FCSTD DOCUMENT  (FreeCAD 0.21R33771 (Git))
Label: ex94
License: All rights reserved
LicenseURL: http://en.wikipedia.org/wiki/All_rights_reserved
objects: Sketcher::SketchObject×2, PartDesign::AdditiveLoft×1, PartDesign::Body×1
note: 5 computed .brp shape members not serialized (recipe doc carries the construction recipe); baked Part::Feature solids carry a one-line shape summary decoded from their .brp

FEATURE [Sketcher::SketchObject] Sketch
  FullyConstrained = false
  MapMode = 5
  Support = -> [XY_Plane]
  sketch-geometry (17):
    g0: LineSegment StartX=0 StartY=-24.175 StartZ=0 EndX=22.9918 EndY=-7.47049 EndZ=0
    g1: LineSegment StartX=22.9918 StartY=-7.47049 StartZ=0 EndX=14.2097 EndY=19.558 EndZ=0
    g2: LineSegment StartX=14.2097 StartY=19.558 StartZ=0 EndX=-14.2097 EndY=19.558 EndZ=0
    g3: LineSegment StartX=-14.2097 StartY=19.558 StartZ=0 EndX=-22.9918 EndY=-7.47049 EndZ=0
    g4: LineSegment StartX=-22.9918 StartY=-7.47049 StartZ=0 EndX=0 EndY=-24.175 EndZ=0
    g5: Circle CenterX=0 CenterY=0 CenterZ=0 NormalX=0 NormalY=0 NormalZ=1 AngleXU=0 Radius=24.175
    g6: LineSegment StartX=-14.2097 StartY=19.558 StartZ=0 EndX=-1.8e-15 EndY=66.3733 EndZ=0
    g7: LineSegment StartX=-1.8e-15 StartY=66.3733 StartZ=0 EndX=14.2097 EndY=19.558 EndZ=0
    g8: LineSegment StartX=14.2097 StartY=19.558 StartZ=0 EndX=63.1247 EndY=20.5105 EndZ=0
    g9: LineSegment StartX=63.1247 StartY=20.5105 StartZ=0 EndX=22.9918 EndY=-7.47049 EndZ=0
    g10: LineSegment StartX=-14.2097 StartY=19.558 StartZ=0 EndX=-63.1247 EndY=20.5105 EndZ=0
    g11: LineSegment StartX=-63.1247 StartY=20.5105 StartZ=0 EndX=-22.9918 EndY=-7.47049 EndZ=0
    g12: LineSegment StartX=-22.9918 StartY=-7.47049 StartZ=0 EndX=-39.0132 EndY=-53.6971 EndZ=0
    g13: LineSegment StartX=-39.0132 StartY=-53.6971 StartZ=0 EndX=0 EndY=-24.175 EndZ=0
    g14: LineSegment StartX=0 StartY=-24.175 StartZ=0 EndX=39.0132 EndY=-53.6971 EndZ=0
    g15: LineSegment StartX=22.9918 StartY=-7.47049 StartZ=0 EndX=39.0132 EndY=-53.6971 EndZ=0
    g16: Circle CenterX=0 CenterY=0 CenterZ=0 NormalX=0 NormalY=0 NormalZ=1 AngleXU=0 Radius=66.3733
  constraints (39):
    c: Coincident(g0,g1)
    c: Coincident(g1,g2)
    c: Coincident(g2,g3)
    c: Coincident(g3,g4)
    c: Coincident(g4,g0)
    c: Equal(g0, g1-g4) x4
    c: PointOnObject(g0,g5)
    c: PointOnObject(g1,g5)
    c: PointOnObject(g2,g5)
    c: PointOnObject(g3,g5)
    c: PointOnObject(g4,g5)
    c: Coincident(g5,g-1)
    c: PointOnObject(g4,g-2)
    c: Coincident(g6,g2)
    c: PointOnObject(g6,g-2)
    c: Coincident(g7,g6)
    c: Coincident(g7,g1)
    c: Coincident(g8,g1)
    c: Coincident(g9,g8)
    c: Coincident(g9,g0)
    c: Coincident(g10,g2)
    c: Coincident(g11,g10)
    c: Coincident(g11,g3)
    c: Coincident(g12,g3)
    c: Coincident(g13,g12)
    c: Coincident(g13,g0)
    c: Coincident(g14,g0)
    c: Coincident(g15,g0)
    c: Coincident(g15,g14)
    c: Equal(g12,g13)
    c: Equal(g14,g15)
    c: Equal(g11,g10)
    c: Equal(g8,g9)
    c: Coincident(g16,g5)
    c: PointOnObject(g14,g16)
    c: PointOnObject(g8,g16)
    c: PointOnObject(g6,g16)
    c: PointOnObject(g10,g16)
    c: PointOnObject(g12,g16)
FEATURE [Sketcher::SketchObject] Sketch001
  AttachmentOffset = pos=(0,0,16) rot=(0,0,1;0rad)
  FullyConstrained = false
  MapMode = 5
  Placement = pos=(0,0,16) rot=(0,0,1;0rad)
  Support = -> [XY_Plane]
  sketch-geometry (1):
    g0: Circle CenterX=0 CenterY=0 CenterZ=0 NormalX=0 NormalY=0 NormalZ=1 AngleXU=0 Radius=2.39644
  constraints (1):
    c: Coincident(g0,g-1)
FEATURE [PartDesign::AdditiveLoft] AdditiveLoft
  Closed = false
  Profile = -> Sketch
  Refine = true
  Ruled = false
  Sections = -> [Sketch001]
FEATURE [PartDesign::Body] Body
  Group = -> [Sketch,Sketch001,AdditiveLoft]
  Origin = -> Origin
  Tip = -> AdditiveLoft
